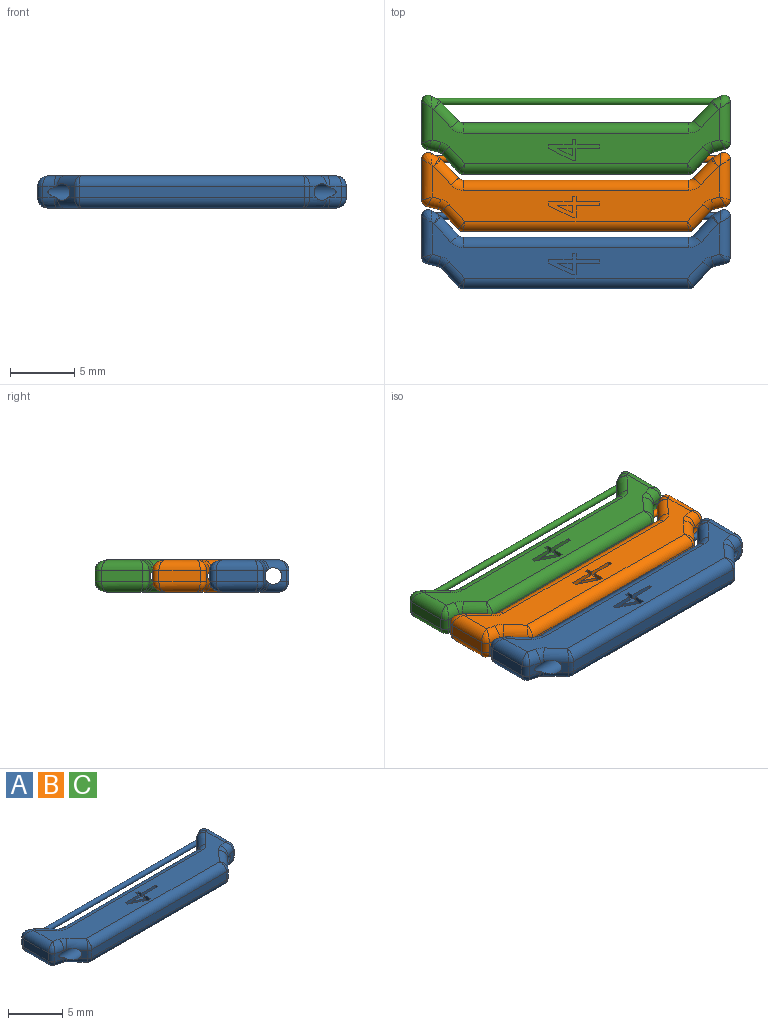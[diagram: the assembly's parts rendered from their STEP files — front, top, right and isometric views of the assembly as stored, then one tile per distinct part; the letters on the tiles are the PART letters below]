
ASSEMBLY  parts=3 mates=2
PART A: 96 faces, bbox 24x6.5x2.5 mm
  f0: plane 22.4x4.33mm, normal (0,0,1), area 49.1mm2, adj f31,f32,f33,f35,f36,f37,f39,f40
  f1: cylinder r=0.5mm len=0.21mm, axis (0,0,-1), area 0mm2, adj f11,f12,f30,f79
  f2: cylinder r=0.5mm len=0.21mm, axis (0,0,-1), area 0mm2, adj f11,f12,f54,f79
  f3: cylinder r=0.5mm len=0.21mm, axis (0,0,-1), area 0mm2, adj f14,f15,f41,f79
  f4: cylinder r=0.5mm len=0.21mm, axis (0,0,-1), area 0mm2, adj f14,f15,f66,f79
  f5: cylinder r=0.5mm len=0.14mm, axis (0,0,1), area 0mm2, adj f9,f42,f78
  f6: cylinder r=0.5mm len=0.14mm, axis (0,0,1), area 0mm2, adj f17,f77,f78
  f7: plane 17.56x0.9mm, normal (0,-1,0), area 15.8mm2, adj f20,f29,f48,f71
  f8: plane 0.9x0.57mm, normal (0.73,-0.68,0), area 0.5mm2, adj f20,f44,f67,f78
  f9: plane 0.91x0.9mm, normal (0.24,-0.97,0), area 0.6mm2, adj f5,f21,f22,f40,f63,f78
  f10: plane 3.2x0.9mm, normal (1,0,0), area 2.9mm2, adj f22,f23,f36,f59
  f11: plane 0.9x0.62mm, normal (-0.49,0.87,0), area 0.5mm2, adj f1,f2,f23,f32,f55,f79
  f12: plane 1.47x1.36mm, normal (-0.73,0.68,0), area 1.7mm2, adj f1,f2,f24,f31,f56,f79
  f13: plane 17.56x0.9mm, normal (0,1,0), area 15.8mm2, adj f24,f25,f35,f60
  f14: plane 1.47x1.36mm, normal (0.73,0.68,0), area 1.7mm2, adj f3,f4,f25,f39,f64,f79
  f15: plane 0.9x0.62mm, normal (0.49,0.87,0), area 0.5mm2, adj f3,f4,f26,f43,f68,f79
  f16: plane 3.2x0.9mm, normal (-1,0,0), area 2.9mm2, adj f26,f27,f47,f72
  f17: plane 0.91x0.9mm, normal (-0.24,-0.97,0), area 0.6mm2, adj f6,f27,f28,f51,f76,f78
  f18: plane 0.9x0.57mm, normal (-0.73,-0.68,0), area 0.5mm2, adj f29,f52,f75,f78
  f19: plane 22.4x4.33mm, normal (0,0,-1), area 51.5mm2, adj f55,f56,f58,f59,f60,f62,f63,f64
  f20: cylinder r=0.5mm len=0.9mm, axis (0,0,1), area 0.4mm2, adj f7,f8,f46,f69
  f21: cylinder r=0.5mm len=0.14mm, axis (0,0,1), area 0mm2, adj f9,f65,f78
  f22: cylinder r=0.5mm len=0.9mm, axis (0,0,-1), area 0.6mm2, adj f9,f10,f38,f61
  f23: cylinder r=0.5mm len=0.9mm, axis (0,0,-1), area 0.9mm2, adj f10,f11,f34,f57
  f24: cylinder r=0.5mm len=0.9mm, axis (0,0,1), area 0.4mm2, adj f12,f13,f33,f58
  f25: cylinder r=0.5mm len=0.9mm, axis (0,0,-1), area 0.4mm2, adj f13,f14,f37,f62
  f26: cylinder r=0.5mm len=0.9mm, axis (0,0,-1), area 0.9mm2, adj f15,f16,f45,f70
  f27: cylinder r=0.5mm len=0.9mm, axis (0,0,-1), area 0.6mm2, adj f16,f17,f49,f74
  f28: cylinder r=0.5mm len=0.14mm, axis (0,0,1), area 0mm2, adj f17,f53,f78
  f29: cylinder r=0.5mm len=0.9mm, axis (0,0,-1), area 0.4mm2, adj f7,f18,f50,f73
  f30: bspline ~0.91x0.67mm, area 0.1mm2, adj f1,f31,f32
  f31: cylinder r=0.8mm len=2.01mm, axis (0.68,0.73,0), area 2.5mm2, adj f0,f12,f30,f33
  f32: cylinder r=0.8mm len=1.05mm, axis (0.87,0.49,0), area 0.6mm2, adj f0,f11,f30,f34
  f33: torus R=1.3mm, axis (0,0,1), area 0.8mm2, adj f0,f24,f31,f35
  f34: bspline ~1.37x1.09mm, area 0.9mm2, adj f23,f32,f36
  f35: cylinder r=0.8mm len=17.56mm, axis (1,0,0), area 22.1mm2, adj f0,f13,f33,f37
  f36: cylinder r=0.8mm len=3.2mm, axis (0,-1,0), area 3.7mm2, adj f0,f10,f34,f38
  f37: torus R=1.3mm, axis (0,0,1), area 0.8mm2, adj f0,f25,f35,f39
  f38: bspline ~0.94x0.8mm, area 0.5mm2, adj f22,f36,f40
  f39: cylinder r=0.8mm len=2.01mm, axis (0.68,-0.73,0), area 2.5mm2, adj f0,f14,f37,f41
  f40: cylinder r=0.8mm len=1.11mm, axis (-0.97,-0.24,0), area 1.1mm2, adj f0,f9,f38,f42
  f41: bspline ~0.91x0.67mm, area 0.1mm2, adj f3,f39,f43
  f42: torus R=1.3mm, axis (0,0,1), area 0.6mm2, adj f0,f5,f40,f44,f78
  f43: cylinder r=0.8mm len=1.05mm, axis (0.87,-0.49,0), area 0.6mm2, adj f0,f15,f41,f45
  f44: cylinder r=0.8mm len=1.96mm, axis (-0.68,-0.73,0), area 2.2mm2, adj f0,f8,f42,f46,f78
  f45: bspline ~1.37x1.09mm, area 0.9mm2, adj f26,f43,f47
  f46: bspline ~0.92x0.8mm, area 0.3mm2, adj f20,f44,f48
  f47: cylinder r=0.8mm len=3.2mm, axis (0,1,0), area 3.7mm2, adj f0,f16,f45,f49
  f48: cylinder r=0.8mm len=17.56mm, axis (-1,0,0), area 22mm2, adj f0,f7,f46,f50
  f49: bspline ~0.94x0.8mm, area 0.5mm2, adj f27,f47,f51
  f50: bspline ~0.92x0.8mm, area 0.3mm2, adj f29,f48,f52
  f51: cylinder r=0.8mm len=1.11mm, axis (-0.97,0.24,0), area 1.1mm2, adj f0,f17,f49,f53
  f52: cylinder r=0.8mm len=1.96mm, axis (-0.68,0.73,0), area 2.2mm2, adj f0,f18,f50,f53,f78
  f53: torus R=1.3mm, axis (0,0,1), area 0.6mm2, adj f0,f28,f51,f52,f78
  f54: bspline ~0.91x0.67mm, area 0.1mm2, adj f2,f55,f56
  f55: cylinder r=0.8mm len=1.05mm, axis (-0.87,-0.49,0), area 0.6mm2, adj f11,f19,f54,f57
  f56: cylinder r=0.8mm len=2.01mm, axis (-0.68,-0.73,0), area 2.5mm2, adj f12,f19,f54,f58
  f57: bspline ~1.37x1.09mm, area 0.9mm2, adj f23,f55,f59
  f58: torus R=1.3mm, axis (0,0,1), area 0.8mm2, adj f19,f24,f56,f60
  f59: cylinder r=0.8mm len=3.2mm, axis (0,1,0), area 3.7mm2, adj f10,f19,f57,f61
  f60: cylinder r=0.8mm len=17.56mm, axis (-1,0,0), area 22.1mm2, adj f13,f19,f58,f62
  f61: bspline ~0.94x0.8mm, area 0.5mm2, adj f22,f59,f63
  f62: torus R=1.3mm, axis (0,0,1), area 0.8mm2, adj f19,f25,f60,f64
  f63: cylinder r=0.8mm len=1.11mm, axis (0.97,0.24,0), area 1.1mm2, adj f9,f19,f61,f65
  f64: cylinder r=0.8mm len=2.01mm, axis (-0.68,0.73,0), area 2.5mm2, adj f14,f19,f62,f66
  f65: torus R=1.3mm, axis (0,0,1), area 0.6mm2, adj f19,f21,f63,f67,f78
  f66: bspline ~0.91x0.67mm, area 0.1mm2, adj f4,f64,f68
  f67: cylinder r=0.8mm len=1.96mm, axis (0.68,0.73,0), area 2.2mm2, adj f8,f19,f65,f69,f78
  f68: cylinder r=0.8mm len=1.05mm, axis (-0.87,0.49,0), area 0.6mm2, adj f15,f19,f66,f70
  f69: bspline ~0.92x0.8mm, area 0.3mm2, adj f20,f67,f71
  f70: bspline ~1.37x1.09mm, area 0.9mm2, adj f26,f68,f72
  f71: cylinder r=0.8mm len=17.56mm, axis (1,0,0), area 22mm2, adj f7,f19,f69,f73
  f72: cylinder r=0.8mm len=3.2mm, axis (0,-1,0), area 3.7mm2, adj f16,f19,f70,f74
  f73: bspline ~0.92x0.8mm, area 0.3mm2, adj f29,f71,f75
  f74: bspline ~0.94x0.8mm, area 0.5mm2, adj f27,f72,f76
  f75: cylinder r=0.8mm len=1.96mm, axis (0.68,-0.73,0), area 2.2mm2, adj f18,f19,f73,f77,f78
  f76: cylinder r=0.8mm len=1.11mm, axis (0.97,-0.24,0), area 1.1mm2, adj f17,f19,f74,f77
  f77: torus R=1.3mm, axis (0,0,1), area 0.6mm2, adj f6,f19,f75,f76,f78
  f78: cylinder r=0.65mm len=22.41mm, axis (1,0,0), area 83.1mm2, adj f5,f6,f8,f9,f17,f18,f21,f28
  f79: cylinder r=0.25mm len=21.9mm, axis (-1,0,0), area 33.3mm2, adj f1,f2,f3,f4,f11,f12,f14,f15
  f80: plane 0.56x0.4mm, normal (1,0,0), area 0.2mm2, adj f81,f93,f94,f95
  f81: plane 1.12x0.56mm, normal (-0.44,-0.9,0), area 0.5mm2, adj f80,f93,f94,f95
  f82: plane 0.43x0.4mm, normal (-1,0,0), area 0.2mm2, adj f0,f83,f92,f94
  f83: plane 0.4x0.3mm, normal (0,-1,0), area 0.1mm2, adj f0,f82,f84,f94
  f84: plane 0.43x0.4mm, normal (1,0,0), area 0.2mm2, adj f0,f83,f85,f94
  f85: plane 1.82x0.4mm, normal (0,-1,0), area 0.7mm2, adj f0,f84,f86,f94
  f86: plane 0.4x0.3mm, normal (1,0,0), area 0.1mm2, adj f0,f85,f87,f94
  f87: plane 1.82x0.9mm, normal (0.44,0.9,0), area 0.8mm2, adj f0,f86,f88,f94
  f88: plane 0.4x0.3mm, normal (0,1,0), area 0.1mm2, adj f0,f87,f89,f94
  f89: plane 0.9x0.4mm, normal (-1,0,0), area 0.4mm2, adj f0,f88,f90,f94
  f90: plane 1.86x0.4mm, normal (0,1,0), area 0.7mm2, adj f0,f89,f91,f94
  f91: plane 0.4x0.3mm, normal (-1,0,0), area 0.1mm2, adj f0,f90,f92,f94
  f92: plane 1.86x0.4mm, normal (0,-1,0), area 0.7mm2, adj f0,f82,f91,f94
  f93: plane 1.12x0.4mm, normal (0,1,0), area 0.4mm2, adj f80,f81,f94,f95
  f94: plane 3.98x1.63mm, normal (0,0,1), area 2.1mm2, adj f80,f81,f82,f83,f84,f85,f86,f87
  f95: plane 1.12x0.56mm, normal (0,0,1), area 0.3mm2, adj f80,f81,f93
PART B: same geometry as A
PART C: same geometry as A
PLACE A t=(9.42,0.94,4.54)mm
PLACE B t=(9.42,5.39,4.54)mm
PLACE C t=(9.42,9.85,4.54)mm
MATE revolute B.f78 <-> A.f79  axis (1,0,0) through (9.42,6.59,4.54)mm
MATE revolute C.f78 <-> B.f79  axis (1,0,0) through (9.42,11.05,4.54)mm
